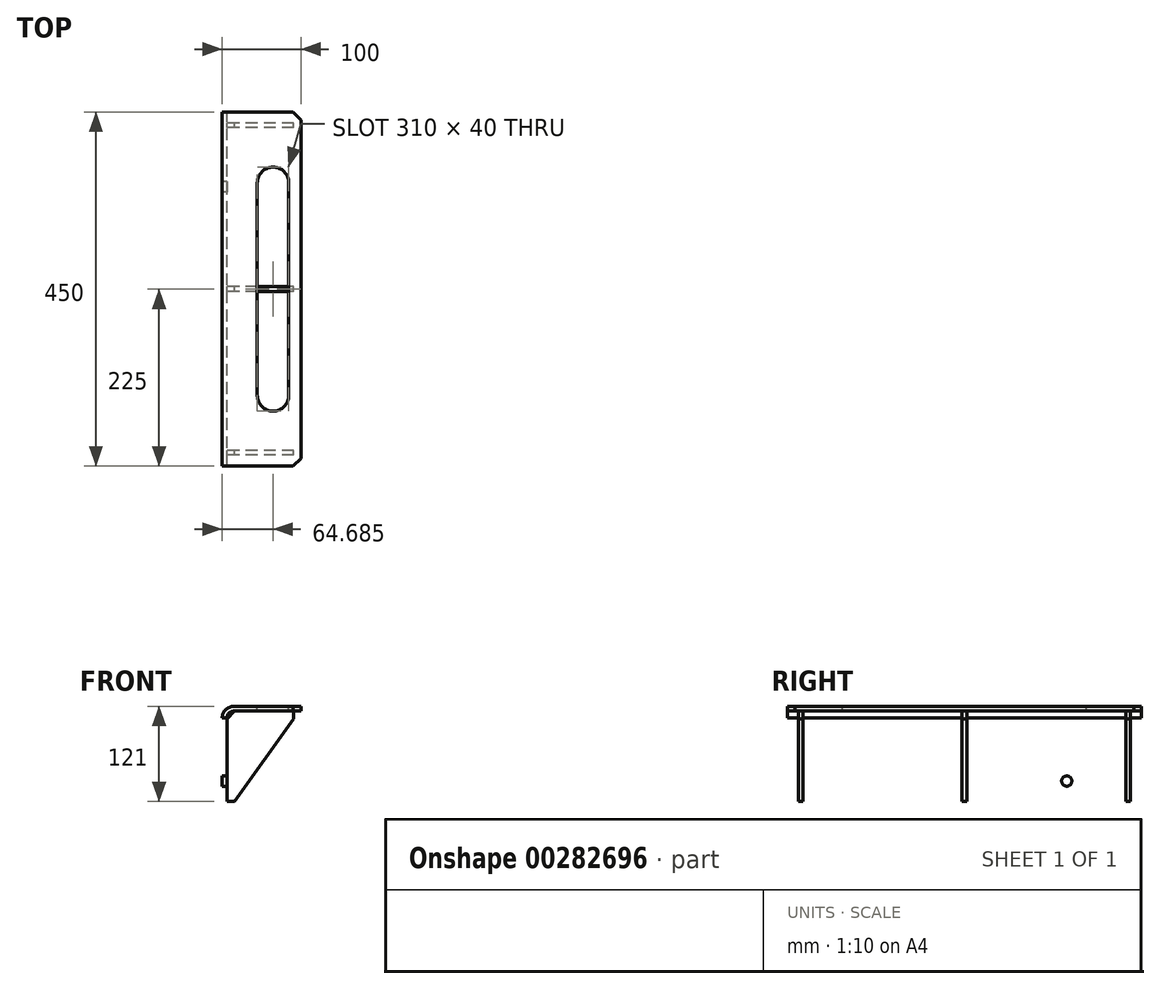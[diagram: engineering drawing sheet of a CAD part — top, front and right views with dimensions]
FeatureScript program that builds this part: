
annotation { "Feature Type Name" : "Feature", "Feature Type Description" : "" }
export const myFeature = defineFeature(function(context is Context, id is Id, definition is map)
    precondition{}
    {
        {
            var Q0;
            Q0=qCreatedBy(makeId("Front.planeOp"),FACE);
            var sketch = newSketch(context, id + "F0", { "sketchPlane" : qUnion([Q0])});
            skLineSegment(sketch, "E0", {"start": v(0, 0) * mm, "end": v(0, 125) * mm});
            skLineSegment(sketch, "E1", {"start": v(15, 140) * mm, "end": v(100, 140) * mm});
            skLineSegment(sketch, "E2.0", {"start": v(15, 134) * mm, "end": v(100, 134) * mm});
            skLineSegment(sketch, "E2.1", {"start": v(6, 0) * mm, "end": v(6, 125) * mm});
            skLineSegment(sketch, "E3", {"start": v(100, 140) * mm, "end": v(100, 134) * mm});
            skLineSegment(sketch, "E4", {"start": v(0, 0) * mm, "end": v(6, 0) * mm});
            skPoint(sketch, "E5.visualSharp", {"position": v(6, 134) * mm});
            skArc(sketch, "E5.filletArc", {"start": v(15, 134) * mm, "mid": v(8.64, 131.36) * mm, "end": v(6, 125) * mm});
            skPoint(sketch, "E6.visualSharp", {"position": v(0, 140) * mm});
            skArc(sketch, "E6.filletArc", {"start": v(15, 140) * mm, "mid": v(4.4, 135.6) * mm, "end": v(0, 125) * mm});
            skSolve(sketch);
        }
        {
            var Q0;
            Q0=makeQuery(id+"F0.imprint","IMPRINT",FACE,{"disambiguationData":[TD([[makeQuery(id+"F0.imprint","IMPRINT",EDGE,{"derivedFrom":sQuery(id+"F0.wireOp",EDGE,"E0")}),-1.0]])]});
            extrude(context, id + "F1", {"entities" : qUnion([Q0]), "depth" : 450 * mm, "symmetric" : true});
        }
        {
            var Q0;
            Q0=makeQuery(id+"F1.opExtrude","SWEPT_FACE",FACE,{"disambiguationData":[OSD([sQuery(id+"F0.wireOp",EDGE,"E2.1")])]});
            var sketch = newSketch(context, id + "F2", { "sketchPlane" : qUnion([Q0])});
            skLineSegment(sketch, "E7.0", {"start": v(-211, 134) * mm, "end": v(-205, 134) * mm});
            skLineSegment(sketch, "E8", {"start": v(-211, 134) * mm, "end": v(-211, 19) * mm});
            skLineSegment(sketch, "E9", {"start": v(-205, 134) * mm, "end": v(-205, 19) * mm});
            skLineSegment(sketch, "E10", {"start": v(-3, 134) * mm, "end": v(-3, 19) * mm});
            skLineSegment(sketch, "E11", {"start": v(3, 134) * mm, "end": v(3, 19) * mm});
            skLineSegment(sketch, "E12", {"start": v(211, 134) * mm, "end": v(211, 19) * mm});
            skLineSegment(sketch, "E13", {"start": v(205, 134) * mm, "end": v(205, 19) * mm});
            skPoint(sketch, "E14.orphan", {"position": v(-225, 134) * mm});
            skLineSegment(sketch, "E15.trimOffspring", {"start": v(-3, 134) * mm, "end": v(3, 134) * mm});
            skLineSegment(sketch, "E16.trimOffspring", {"start": v(205, 134) * mm, "end": v(211, 134) * mm});
            skPoint(sketch, "E17.orphan", {"position": v(225, 134) * mm});
            skPoint(sketch, "E18.orphan", {"position": v(225, 0) * mm});
            skPoint(sketch, "E19.orphan", {"position": v(-225, 0) * mm});
            skLineSegment(sketch, "E20", {"start": v(-211, 19) * mm, "end": v(-205, 19) * mm});
            skLineSegment(sketch, "E21.trimOffspring", {"start": v(-3, 19) * mm, "end": v(3, 19) * mm});
            skLineSegment(sketch, "E22.trimOffspring", {"start": v(205, 19) * mm, "end": v(211, 19) * mm});
            skSolve(sketch);
        }
        {
            var Q0;
            {var subQ0=sQuery(id+"F2.wireOp",EDGE,"E7.0");Q0=makeQuery(id+"F2.imprint","IMPRINT",FACE,{"disambiguationData":[TD([[makeQuery(id+"F2.imprint","IMPRINT",EDGE,{"derivedFrom":subQ0}),-1.0]])]});}
            var Q1;
            {var subQ0=sQuery(id+"F2.wireOp",EDGE,"E20");Q1=makeQuery(id+"F2.imprint","IMPRINT",FACE,{"disambiguationData":[TD([[makeQuery(id+"F2.imprint","IMPRINT",EDGE,{"derivedFrom":subQ0}),1.0]])]});}
            var Q2;
            {var subQ0=sQuery(id+"F2.wireOp",EDGE,"E15.trimOffspring");Q2=makeQuery(id+"F2.imprint","IMPRINT",FACE,{"disambiguationData":[TD([[makeQuery(id+"F2.imprint","IMPRINT",EDGE,{"derivedFrom":subQ0}),-1.0]])]});}
            var Q3;
            {var subQ0=sQuery(id+"F2.wireOp",EDGE,"E21.trimOffspring");Q3=makeQuery(id+"F2.imprint","IMPRINT",FACE,{"disambiguationData":[TD([[makeQuery(id+"F2.imprint","IMPRINT",EDGE,{"derivedFrom":subQ0}),1.0]])]});}
            var Q4;
            {var subQ0=sQuery(id+"F2.wireOp",EDGE,"E22.trimOffspring");Q4=makeQuery(id+"F2.imprint","IMPRINT",FACE,{"disambiguationData":[TD([[makeQuery(id+"F2.imprint","IMPRINT",EDGE,{"derivedFrom":subQ0}),1.0]])]});}
            var Q5;
            {var subQ0=sQuery(id+"F2.wireOp",EDGE,"E16.trimOffspring");Q5=makeQuery(id+"F2.imprint","IMPRINT",FACE,{"disambiguationData":[TD([[makeQuery(id+"F2.imprint","IMPRINT",EDGE,{"derivedFrom":subQ0}),-1.0]])]});}
            extrude(context, id + "F3", {"entities" : qUnion([Q0, Q1, Q2, Q3, Q4, Q5]), "depth" : 85 * mm});
        }
        {
            var Q0;
            Q0=makeQuery(id+"F3.opExtrude","CAP_EDGE",EDGE,{"disambiguationData":[OSD([sQuery(id+"F2.wireOp",EDGE,"E16.trimOffspring")])],"isStart":true});
            var Q1;
            Q1=makeQuery(id+"F3.opExtrude","CAP_EDGE",EDGE,{"disambiguationData":[OSD([sQuery(id+"F2.wireOp",EDGE,"E15.trimOffspring")])],"isStart":true});
            var Q2;
            Q2=makeQuery(id+"F3.opExtrude","CAP_EDGE",EDGE,{"disambiguationData":[OSD([sQuery(id+"F2.wireOp",EDGE,"E7.0")])],"isStart":true});
            chamfer(context, id + "F4", {"entities" : qUnion([Q0, Q1, Q2]), "width" : 10 * mm, "tangentPropagation" : true});
        }
        {
            var Q0;
            Q0=makeQuery(id+"F3.opExtrude","SWEPT_FACE",FACE,{"disambiguationData":[OSD([sQuery(id+"F2.wireOp",EDGE,"E12")])]});
            var sketch = newSketch(context, id + "F5", { "sketchPlane" : qUnion([Q0])});
            skLineSegment(sketch, "E23", {"start": v(-91, 124) * mm, "end": v(-16, 19) * mm});
            skSolve(sketch);
        }
        {
            var Q0;
            {var subQ0=sQuery(id+"F5.wireOp",EDGE,"E23");Q0=makeQuery(id+"F5.imprint","IMPRINT",FACE,{"disambiguationData":[TD([[makeQuery(id+"F5.imprint","IMPRINT",EDGE,{"derivedFrom":subQ0}),-1.0]])]});}
            extrude(context, id + "F6", {"entities" : qUnion([Q0]), "operationType" : NewBodyOperationType.REMOVE, "oppositeDirection" : true, "depth" : 450 * mm});
        }
        {
            var Q0;
            Q0=makeQuery(id+"F1.opExtrude","CAP_EDGE",EDGE,{"disambiguationData":[OSD([sQuery(id+"F0.wireOp",EDGE,"E3")])],"isStart":true});
            var Q1;
            Q1=makeQuery(id+"F1.opExtrude","CAP_EDGE",EDGE,{"disambiguationData":[OSD([sQuery(id+"F0.wireOp",EDGE,"E4")])],"isStart":true});
            var Q2;
            Q2=makeQuery(id+"F1.opExtrude","CAP_EDGE",EDGE,{"disambiguationData":[OSD([sQuery(id+"F0.wireOp",EDGE,"E3")])],"isStart":false});
            var Q3;
            Q3=makeQuery(id+"F1.opExtrude","CAP_EDGE",EDGE,{"disambiguationData":[OSD([sQuery(id+"F0.wireOp",EDGE,"E4")])],"isStart":false});
            chamfer(context, id + "F7", {"entities" : qUnion([Q0, Q1, Q2, Q3]), "width" : 10 * mm, "tangentPropagation" : true});
        }
        {
            var Q0;
            Q0=makeQuery(id+"F1.opExtrude","SWEPT_FACE",FACE,{"disambiguationData":[OSD([sQuery(id+"F0.wireOp",EDGE,"E1")])]});
            var sketch = newSketch(context, id + "F8", { "sketchPlane" : qUnion([Q0])});
            skLineSegment(sketch, "E24", {"start": v(64.68, 225) * mm, "end": v(64.68, -225) * mm, "construction": true});
            skArc(sketch, "E25", {"start": v(84.68, 135) * mm, "mid": v(64.68, 155) * mm, "end": v(44.68, 135) * mm});
            skArc(sketch, "E26", {"start": v(44.68, -135) * mm, "mid": v(64.68, -155) * mm, "end": v(84.68, -135) * mm});
            skLineSegment(sketch, "E27", {"start": v(44.68, 135) * mm, "end": v(44.68, -135) * mm});
            skLineSegment(sketch, "E28", {"start": v(84.68, 135) * mm, "end": v(84.68, -135) * mm});
            skSolve(sketch);
        }
        {
            var Q0;
            Q0=makeQuery(id+"F8.imprint","IMPRINT",FACE,{"disambiguationData":[TD([[makeQuery(id+"F8.imprint","IMPRINT",EDGE,{"derivedFrom":sQuery(id+"F8.wireOp",EDGE,"E25")}),1.0]])]});
            extrude(context, id + "F9", {"entities" : qUnion([Q0]), "operationType" : NewBodyOperationType.REMOVE, "oppositeDirection" : true, "depth" : 6 * mm});
        }
        {
            var Q0;
            Q0=makeQuery(id+"F1.opExtrude","SWEPT_FACE",FACE,{"disambiguationData":[OSD([sQuery(id+"F0.wireOp",EDGE,"E0")])]});
            var sketch = newSketch(context, id + "F10", { "sketchPlane" : qUnion([Q0])});
            skCircle(sketch, "E29", {"center": v(130, 45) * mm, "radius": 6.5 * mm});
            skCircle(sketch, "E30.MirrorC", {"center": v(-130, 45) * mm, "radius": 6.5 * mm});
            skSolve(sketch);
        }
        {
            var Q0;
            Q0=makeQuery(id+"F10.imprint","IMPRINT",FACE,{"disambiguationData":[TD([[makeQuery(id+"F10.imprint","IMPRINT",EDGE,{"derivedFrom":sQuery(id+"F10.wireOp",EDGE,"E30.MirrorC")}),-1.0]])]});
            var Q1;
            Q1=makeQuery(id+"F10.imprint","IMPRINT",FACE,{"disambiguationData":[TD([[makeQuery(id+"F10.imprint","IMPRINT",EDGE,{"derivedFrom":sQuery(id+"F10.wireOp",EDGE,"E29")}),1.0]])]});
            extrude(context, id + "F11", {"entities" : qUnion([Q0, Q1]), "operationType" : NewBodyOperationType.REMOVE, "oppositeDirection" : true, "depth" : 6 * mm});
        }
    });
